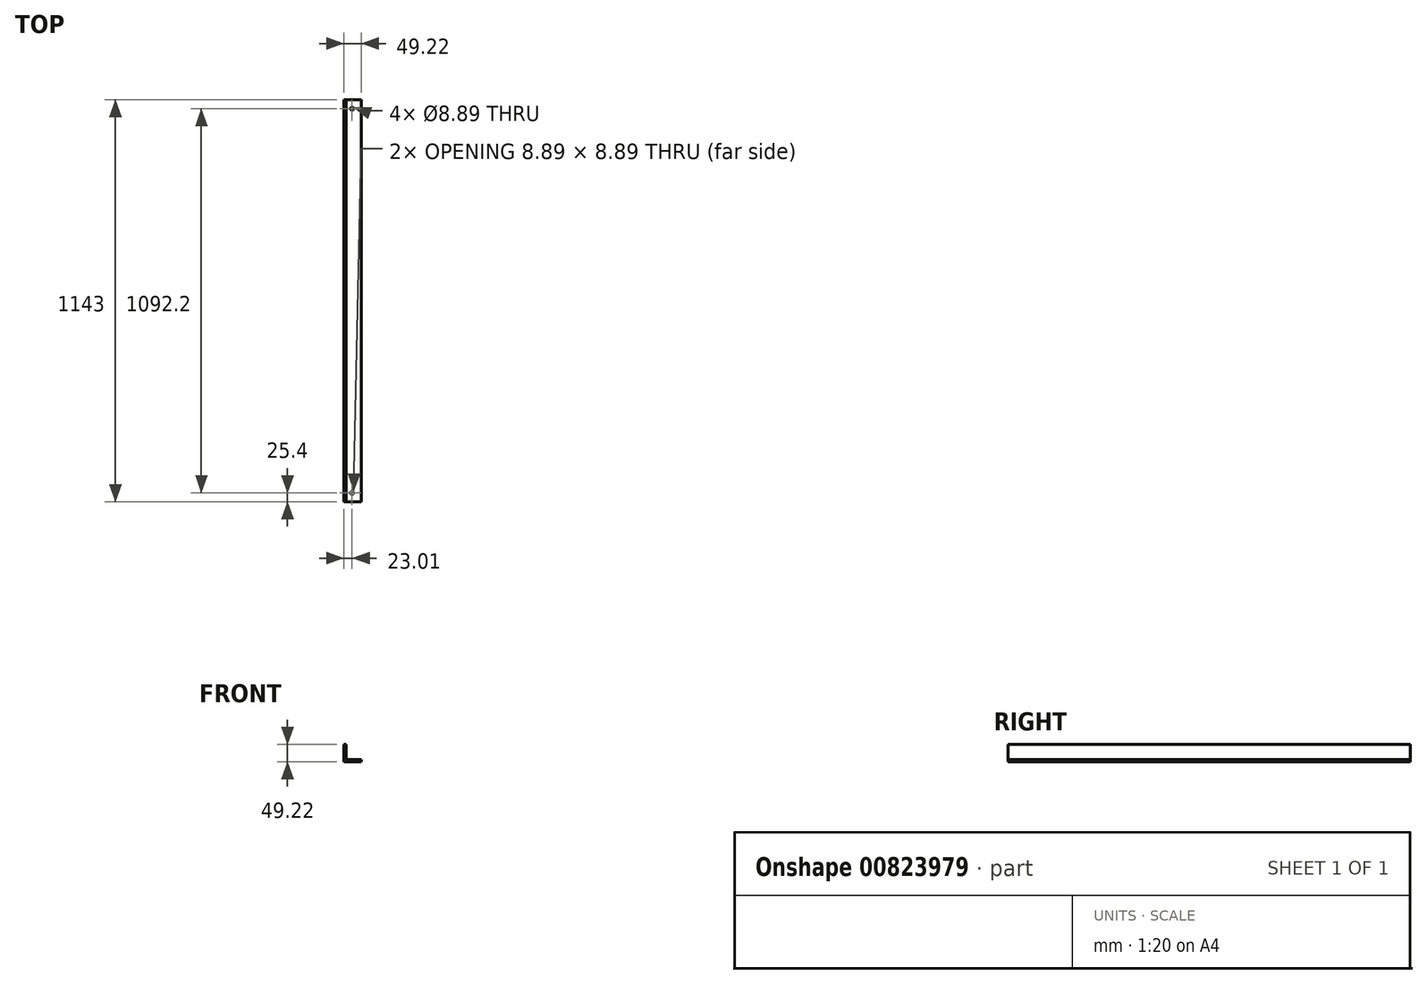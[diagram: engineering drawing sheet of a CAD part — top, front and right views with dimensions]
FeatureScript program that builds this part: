
annotation { "Feature Type Name" : "Feature", "Feature Type Description" : "" }
export const myFeature = defineFeature(function(context is Context, id is Id, definition is map)
    precondition{}
    {
        {
            var Q0;
            Q0=qCreatedBy(makeId("Front.planeOp"),FACE);
            var sketch = newSketch(context, id + "F0", { "sketchPlane" : qUnion([Q0])});
            skLineSegment(sketch, "E0.bottom", {"start": v(24.61, -24.61) * mm, "end": v(-24.61, -24.61) * mm});
            skLineSegment(sketch, "E0.top", {"start": v(-18.26, 24.61) * mm, "end": v(-24.61, 24.61) * mm});
            skLineSegment(sketch, "E0.left", {"start": v(24.61, -24.61) * mm, "end": v(24.61, -18.26) * mm});
            skLineSegment(sketch, "E0.right", {"start": v(-24.61, -24.61) * mm, "end": v(-24.61, 24.61) * mm});
            skPoint(sketch, "E0.middle", {"position": v(0, 0) * mm});
            skLineSegment(sketch, "E1", {"start": v(-18.26, 24.61) * mm, "end": v(-18.26, -18.26) * mm});
            skLineSegment(sketch, "E2", {"start": v(-18.26, -18.26) * mm, "end": v(24.61, -18.26) * mm});
            skSolve(sketch);
        }
        {
            var Q0;
            Q0=makeQuery(id+"F0.imprint","IMPRINT",FACE,{"disambiguationData":[TD([[makeQuery(id+"F0.imprint","IMPRINT",EDGE,{"derivedFrom":sQuery(id+"F0.wireOp",EDGE,"E0.bottom")}),-1.0]])]});
            extrude(context, id + "F1", {"entities" : qUnion([Q0]), "endBound" : BoundingType.SYMMETRIC, "depth" : 1143 * mm, "offsetDistance" : 25.4 * mm});
        }
        {
            var Q0;
            Q0=makeQuery(id+"F1.opExtrude","SWEPT_FACE",FACE,{"disambiguationData":[OSD([sQuery(id+"F0.wireOp",EDGE,"E2")])]});
            var sketch = newSketch(context, id + "F2", { "sketchPlane" : qUnion([Q0])});
            skCircle(sketch, "E3", {"center": v(-1.6, -546.1) * mm, "radius": 4.76 * mm});
            skCircle(sketch, "E4.MirrorC", {"center": v(-1.6, 546.1) * mm, "radius": 4.76 * mm});
            skLineSegment(sketch, "E5", {"start": v(0, -711.48) * mm, "end": v(0, 689.84) * mm, "construction": true});
            skSolve(sketch);
        }
        {
            var Q0;
            Q0=sQuery(id+"F2.wireOp",VERTEX,"E3.center");
            var Q1;
            Q1=sQuery(id+"F2.wireOp",VERTEX,"E4.MirrorC.center");
            var Q2;
            Q2=makeQuery(id+"F1.opExtrude","SWEPT_BODY",BODY,{"disambiguationData":[OSD([sQuery(id+"F0.wireOp",EDGE,"E0.bottom"),sQuery(id+"F0.wireOp",EDGE,"E0.top"),sQuery(id+"F0.wireOp",EDGE,"E0.left"),sQuery(id+"F0.wireOp",EDGE,"E0.right"),sQuery(id+"F0.wireOp",EDGE,"E1"),sQuery(id+"F0.wireOp",EDGE,"E2")])]});
            hole(context, id + "F3", {"style" : HoleStyle.SIMPLE, "endStyle" : HoleEndStyle.THROUGH, "holeDiameter" : 8.9 * mm, "majorDiameter" : 6.35 * mm, "isTappedThrough" : true, "tappedDepth" : 12.7 * mm, "tapClearance" : 3, "locations" : qUnion([Q0, Q1]), "scope" : qUnion([Q2])});
        }
    });
